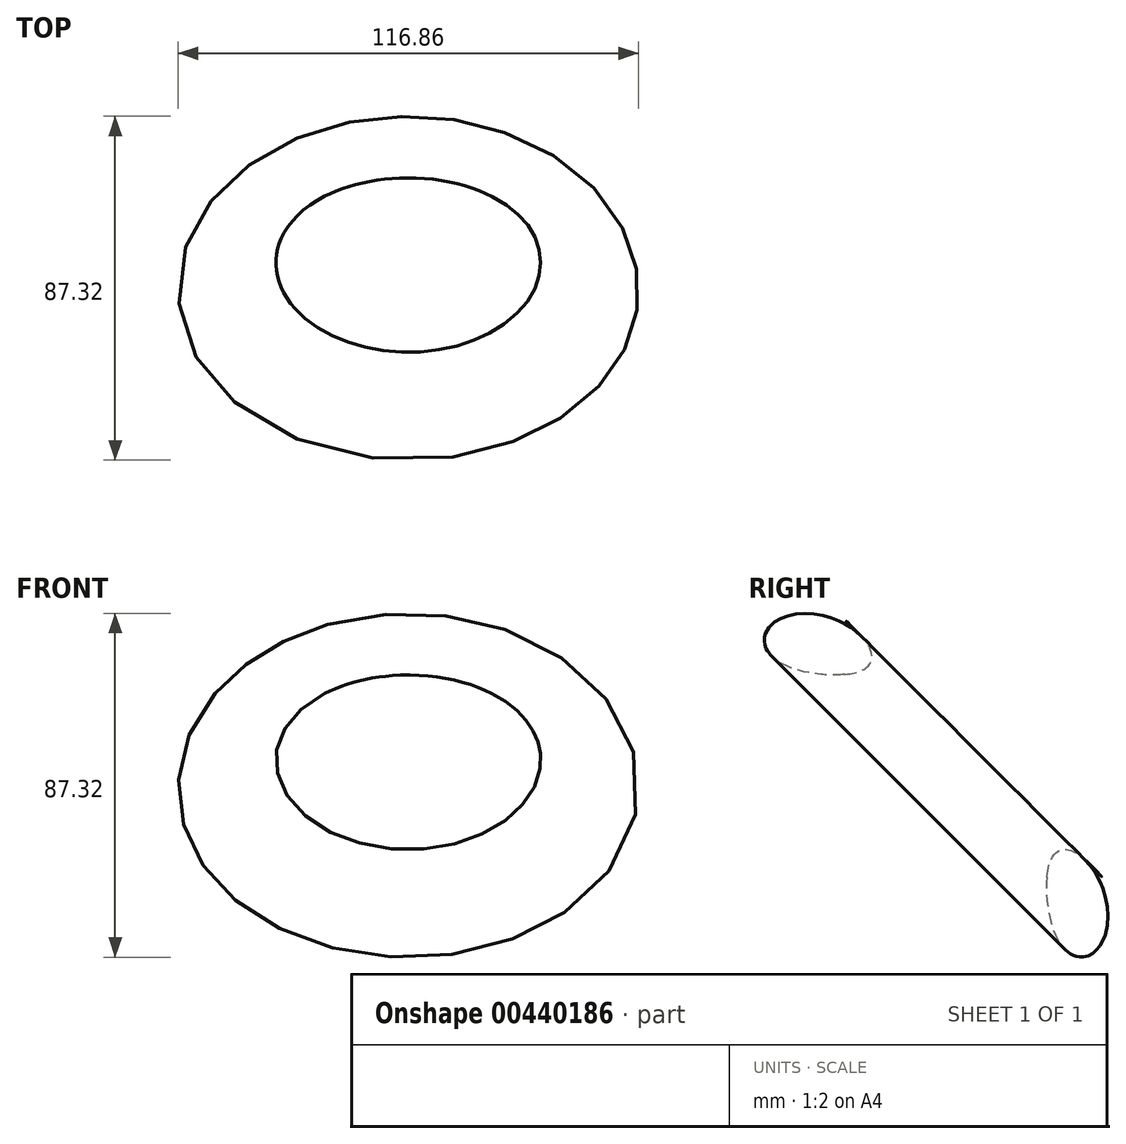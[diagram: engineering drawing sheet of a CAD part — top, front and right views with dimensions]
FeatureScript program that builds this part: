
annotation { "Feature Type Name" : "Feature", "Feature Type Description" : "" }
export const myFeature = defineFeature(function(context is Context, id is Id, definition is map)
    precondition{}
    {
        {
            var Q0;
            Q0=qCreatedBy(makeId("Top.planeOp"),FACE);
            var sketch = newSketch(context, id + "F0", { "sketchPlane" : qUnion([Q0])});
            skCircle(sketch, "E0", {"center": v(-35.16, -41.67) * mm, "radius": 13.92 * mm});
            skSolve(sketch);
        }
        {
            var Q0;
            Q0=qCreatedBy(makeId("Right.planeOp"),FACE);
            var sketch = newSketch(context, id + "F1", { "sketchPlane" : qUnion([Q0])});
            skLineSegment(sketch, "E1", {"start": v(0, 0) * mm, "end": v(36.5, 36.5) * mm});
            skLineSegment(sketch, "E2", {"start": v(0, 0) * mm, "end": v(44.22, 0) * mm});
            skSolve(sketch);
        }
        {
            var Q0;
            Q0=makeQuery(id+"F0.imprint","IMPRINT",FACE,{"disambiguationData":[TD([[makeQuery(id+"F0.imprint","IMPRINT",EDGE,{"derivedFrom":sQuery(id+"F0.wireOp",EDGE,"E0")}),1.0]])]});
            var Q1;
            Q1=sQuery(id+"F1.wireOp",EDGE,"E1");
            revolve(context, id + "F2", {"entities" : qUnion([Q0]), "axis" : qUnion([Q1]), "revolveType" : RevolveType.FULL});
        }
    });
